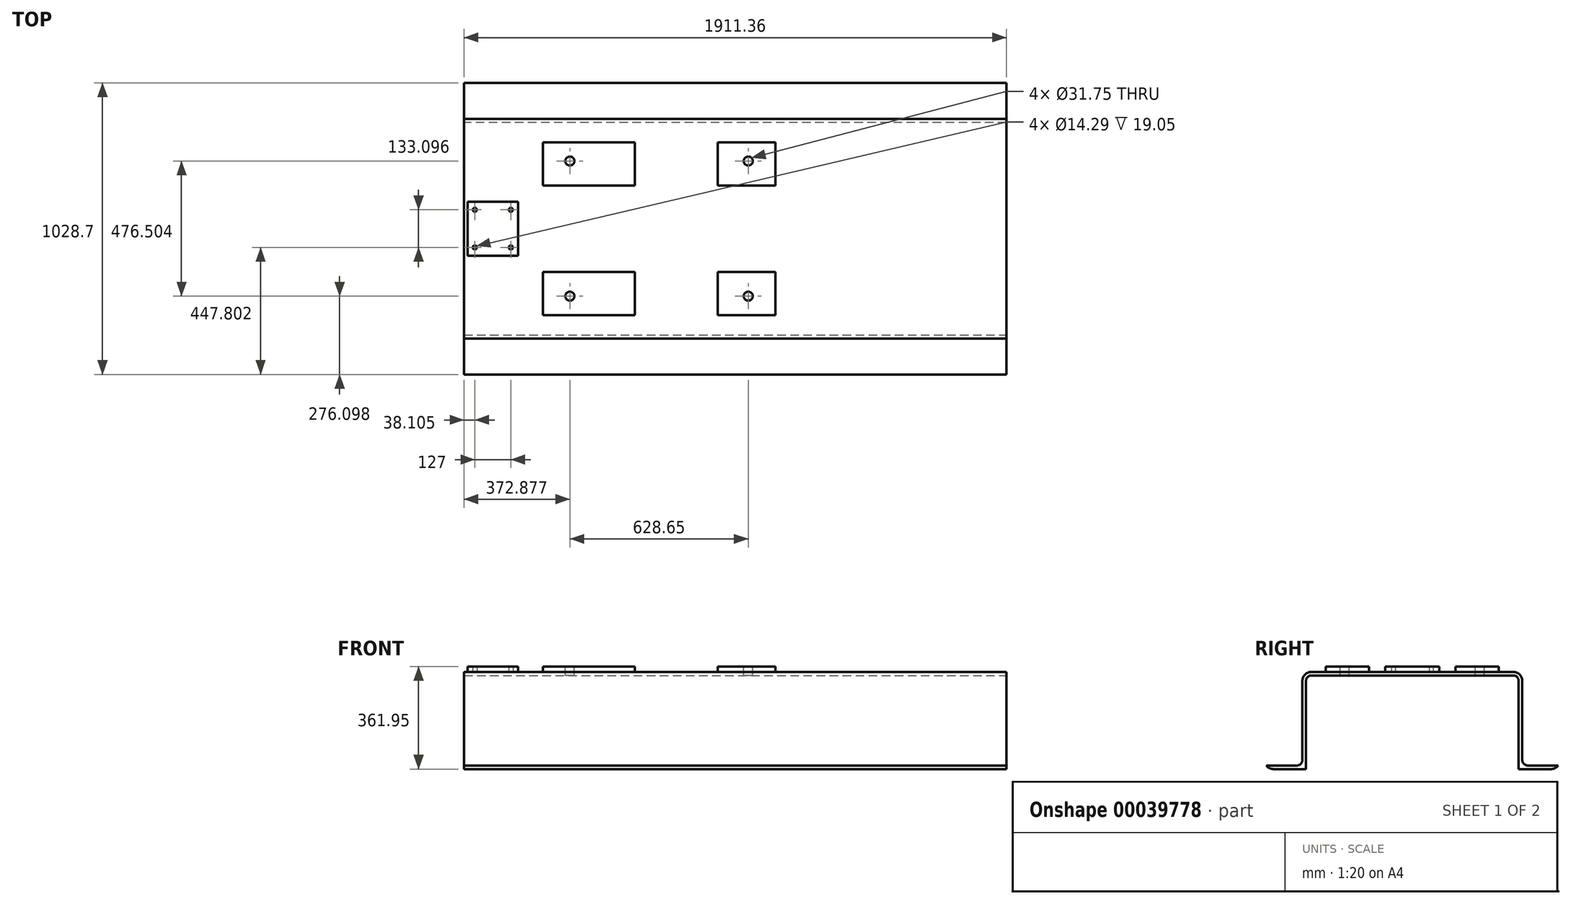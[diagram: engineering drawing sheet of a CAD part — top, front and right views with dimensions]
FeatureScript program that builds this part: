
annotation { "Feature Type Name" : "Feature", "Feature Type Description" : "" }
export const myFeature = defineFeature(function(context is Context, id is Id, definition is map)
    precondition{}
    {
        {
            var Q0;
            Q0=qCreatedBy(makeId("Top.planeOp"),FACE);
            var sketch = newSketch(context, id + "F0", { "sketchPlane" : qUnion([Q0])});
            skLineSegment(sketch, "E0.rect.bottom", {"start": v(-955.68, 387.35) * mm, "end": v(955.68, 387.35) * mm});
            skLineSegment(sketch, "E0.rect.top", {"start": v(-955.68, -387.35) * mm, "end": v(955.68, -387.35) * mm});
            skLineSegment(sketch, "E0.rect.left", {"start": v(-955.68, 387.35) * mm, "end": v(-955.68, -387.35) * mm});
            skLineSegment(sketch, "E0.rect.right", {"start": v(955.68, 387.35) * mm, "end": v(955.68, -387.35) * mm});
            skPoint(sketch, "E0.rect.middle", {"position": v(0, 0) * mm});
            skLineSegment(sketch, "E1.0", {"start": v(644.53, 387.35) * mm, "end": v(644.52, -387.35) * mm, "construction": true});
            skLineSegment(sketch, "E2.0", {"start": v(-268.35, 387.35) * mm, "end": v(-268.35, -387.35) * mm, "construction": true});
            skLineSegment(sketch, "E3.0", {"start": v(-354.2, 387.35) * mm, "end": v(-354.2, -387.35) * mm, "construction": true});
            skLineSegment(sketch, "E4.0", {"start": v(-678.05, 387.35) * mm, "end": v(-678.05, -387.35) * mm, "construction": true});
            skLineSegment(sketch, "E5.0", {"start": v(-62.1, 387.35) * mm, "end": v(-62.1, -387.35) * mm, "construction": true});
            skLineSegment(sketch, "E6.0", {"start": v(141.1, 387.35) * mm, "end": v(141.1, -387.35) * mm, "construction": true});
            skLineSegment(sketch, "E7", {"start": v(-955.68, 0) * mm, "end": v(955.68, 0) * mm, "construction": true});
            skLineSegment(sketch, "E8.0", {"start": v(-955.68, -152.4) * mm, "end": v(955.68, -152.4) * mm, "construction": true});
            skLineSegment(sketch, "E9.0", {"start": v(-955.68, -304.8) * mm, "end": v(955.68, -304.8) * mm, "construction": true});
            skLineSegment(sketch, "E10.bottom", {"start": v(-678.05, -152.4) * mm, "end": v(-354.2, -152.4) * mm});
            skLineSegment(sketch, "E10.top", {"start": v(-678.05, -304.8) * mm, "end": v(-354.2, -304.8) * mm});
            skLineSegment(sketch, "E10.left", {"start": v(-678.05, -152.4) * mm, "end": v(-678.05, -304.8) * mm});
            skLineSegment(sketch, "E10.right", {"start": v(-354.2, -152.4) * mm, "end": v(-354.2, -304.8) * mm});
            skLineSegment(sketch, "E11.bottom", {"start": v(-62.1, -152.4) * mm, "end": v(141.1, -152.4) * mm});
            skLineSegment(sketch, "E11.top", {"start": v(-62.1, -304.8) * mm, "end": v(141.1, -304.8) * mm});
            skLineSegment(sketch, "E11.left", {"start": v(-62.1, -152.4) * mm, "end": v(-62.1, -304.8) * mm});
            skLineSegment(sketch, "E11.right", {"start": v(141.1, -152.4) * mm, "end": v(141.1, -304.8) * mm});
            skLineSegment(sketch, "E12.0", {"start": v(-582.8, 387.35) * mm, "end": v(-582.8, -387.35) * mm, "construction": true});
            skLineSegment(sketch, "E13.0", {"start": v(45.85, 387.35) * mm, "end": v(45.85, -387.35) * mm, "construction": true});
            skLineSegment(sketch, "E14.0", {"start": v(-955.68, -238.25) * mm, "end": v(955.68, -238.25) * mm, "construction": true});
            skCircle(sketch, "E15", {"center": v(-582.8, -238.25) * mm, "radius": 15.88 * mm});
            skCircle(sketch, "E16", {"center": v(45.85, -238.25) * mm, "radius": 15.88 * mm});
            skLineSegment(sketch, "E17.MirrorCS", {"start": v(-354.2, 152.4) * mm, "end": v(-354.2, 304.8) * mm});
            skLineSegment(sketch, "E18.MirrorCS", {"start": v(-62.1, 304.8) * mm, "end": v(141.1, 304.8) * mm});
            skLineSegment(sketch, "E19.MirrorCS", {"start": v(141.1, 152.4) * mm, "end": v(141.1, 304.8) * mm});
            skCircle(sketch, "E20.MirrorC", {"center": v(45.85, 238.25) * mm, "radius": 15.88 * mm});
            skCircle(sketch, "E21.MirrorC", {"center": v(-582.8, 238.25) * mm, "radius": 15.88 * mm});
            skLineSegment(sketch, "E22.MirrorCS", {"start": v(-62.1, 152.4) * mm, "end": v(-62.1, 304.8) * mm});
            skLineSegment(sketch, "E23.MirrorCS", {"start": v(-678.05, 152.4) * mm, "end": v(-354.2, 152.4) * mm});
            skLineSegment(sketch, "E24.MirrorCS", {"start": v(-678.05, 152.4) * mm, "end": v(-678.05, 304.8) * mm});
            skLineSegment(sketch, "E25.MirrorCS", {"start": v(-62.1, 152.4) * mm, "end": v(141.1, 152.4) * mm});
            skLineSegment(sketch, "E26.MirrorCS", {"start": v(-678.05, 304.8) * mm, "end": v(-354.2, 304.8) * mm});
            skSolve(sketch);
        }
        {
            var Q0;
            Q0=makeQuery(id+"F0.imprint","IMPRINT",FACE,{"disambiguationData":[TD([[makeQuery(id+"F0.imprint","IMPRINT",EDGE,{"derivedFrom":sQuery(id+"F0.wireOp",EDGE,"E0.rect.bottom")}),-1.0]])]});
            var Q1;
            Q1=makeQuery(id+"F0.imprint","IMPRINT",FACE,{"disambiguationData":[TD([[makeQuery(id+"F0.imprint","IMPRINT",EDGE,{"derivedFrom":sQuery(id+"F0.wireOp",EDGE,"E17.MirrorCS")}),1.0]])]});
            var Q2;
            Q2=makeQuery(id+"F0.imprint","IMPRINT",FACE,{"disambiguationData":[TD([[makeQuery(id+"F0.imprint","IMPRINT",EDGE,{"derivedFrom":sQuery(id+"F0.wireOp",EDGE,"E10.bottom")}),-1.0]])]});
            var Q3;
            Q3=makeQuery(id+"F0.imprint","IMPRINT",FACE,{"disambiguationData":[TD([[makeQuery(id+"F0.imprint","IMPRINT",EDGE,{"derivedFrom":sQuery(id+"F0.wireOp",EDGE,"E18.MirrorCS")}),-1.0]])]});
            var Q4;
            Q4=makeQuery(id+"F0.imprint","IMPRINT",FACE,{"disambiguationData":[TD([[makeQuery(id+"F0.imprint","IMPRINT",EDGE,{"derivedFrom":sQuery(id+"F0.wireOp",EDGE,"E11.bottom")}),-1.0]])]});
            extrude(context, id + "F1", {"entities" : qUnion([Q0, Q1, Q2, Q3, Q4]), "oppositeDirection" : true, "depth" : 12.7 * mm});
        }
        {
            var Q0;
            Q0=makeQuery(id+"F0.imprint","IMPRINT",FACE,{"disambiguationData":[TD([[makeQuery(id+"F0.imprint","IMPRINT",EDGE,{"derivedFrom":sQuery(id+"F0.wireOp",EDGE,"E17.MirrorCS")}),1.0]])]});
            var Q1;
            Q1=makeQuery(id+"F0.imprint","IMPRINT",FACE,{"disambiguationData":[TD([[makeQuery(id+"F0.imprint","IMPRINT",EDGE,{"derivedFrom":sQuery(id+"F0.wireOp",EDGE,"E10.bottom")}),-1.0]])]});
            var Q2;
            Q2=makeQuery(id+"F0.imprint","IMPRINT",FACE,{"disambiguationData":[TD([[makeQuery(id+"F0.imprint","IMPRINT",EDGE,{"derivedFrom":sQuery(id+"F0.wireOp",EDGE,"E18.MirrorCS")}),-1.0]])]});
            var Q3;
            Q3=makeQuery(id+"F0.imprint","IMPRINT",FACE,{"disambiguationData":[TD([[makeQuery(id+"F0.imprint","IMPRINT",EDGE,{"derivedFrom":sQuery(id+"F0.wireOp",EDGE,"E11.bottom")}),-1.0]])]});
            extrude(context, id + "F2", {"entities" : qUnion([Q0, Q1, Q2, Q3]), "operationType" : NewBodyOperationType.ADD, "depth" : 19.05 * mm});
        }
        {
            var Q0;
            Q0=makeQuery(id+"F1.opExtrude","SWEPT_FACE",FACE,{"disambiguationData":[OSD([sQuery(id+"F0.wireOp",EDGE,"E0.rect.right")])]});
            var sketch = newSketch(context, id + "F3", { "sketchPlane" : qUnion([Q0])});
            skLineSegment(sketch, "E27.bottom", {"start": v(-387.35, 0) * mm, "end": v(-374.65, 0) * mm});
            skLineSegment(sketch, "E27.top", {"start": v(-387.35, -342.9) * mm, "end": v(-374.65, -342.9) * mm});
            skLineSegment(sketch, "E27.left", {"start": v(-387.35, 0) * mm, "end": v(-387.35, -342.9) * mm});
            skLineSegment(sketch, "E27.right", {"start": v(-374.65, 0) * mm, "end": v(-374.65, -342.9) * mm});
            skLineSegment(sketch, "E28", {"start": v(0, 0) * mm, "end": v(0, -288.05) * mm, "construction": true});
            skPoint(sketch, "E28.endSnap0", {"position": v(0, -12.7) * mm});
            skLineSegment(sketch, "E29.bottom", {"start": v(-374.65, -342.9) * mm, "end": v(-514.35, -342.9) * mm});
            skLineSegment(sketch, "E29.top", {"start": v(-374.65, -330.2) * mm, "end": v(-514.35, -330.2) * mm});
            skLineSegment(sketch, "E29.left", {"start": v(-374.65, -342.9) * mm, "end": v(-374.65, -330.2) * mm});
            skLineSegment(sketch, "E29.right", {"start": v(-514.35, -342.9) * mm, "end": v(-514.35, -330.2) * mm});
            skLineSegment(sketch, "E30.MirrorCS", {"start": v(387.35, 0) * mm, "end": v(374.65, 0) * mm});
            skLineSegment(sketch, "E31.MirrorCS", {"start": v(374.65, -342.9) * mm, "end": v(374.65, -330.2) * mm});
            skLineSegment(sketch, "E32.MirrorCS", {"start": v(387.35, -342.9) * mm, "end": v(374.65, -342.9) * mm});
            skLineSegment(sketch, "E33.MirrorCS", {"start": v(514.35, -342.9) * mm, "end": v(514.35, -330.2) * mm});
            skLineSegment(sketch, "E34.MirrorCS", {"start": v(387.35, 0) * mm, "end": v(387.35, -342.9) * mm});
            skLineSegment(sketch, "E35.MirrorCS", {"start": v(374.65, 0) * mm, "end": v(374.65, -342.9) * mm});
            skLineSegment(sketch, "E36.MirrorCS", {"start": v(374.65, -330.2) * mm, "end": v(514.35, -330.2) * mm});
            skLineSegment(sketch, "E37.MirrorCS", {"start": v(374.65, -342.9) * mm, "end": v(514.35, -342.9) * mm});
            skSolve(sketch);
        }
        {
            var Q0;
            Q0 = qSketchRegion(id + "F3", true);
            extrude(context, id + "F4", {"entities" : qUnion([Q0]), "operationType" : NewBodyOperationType.ADD, "oppositeDirection" : true, "depth" : 1911.35 * mm});
        }
        {
            var Q0;
            Q0=makeQuery(id+"F4.opExtrude","SWEPT_EDGE",EDGE,{"disambiguationData":[OSD([sQuery(id+"F3.wireOp",EDGE,"E27.left"),sQuery(id+"F3.wireOp",EDGE,"E29.top")])]});
            var Q1;
            Q1=makeQuery(id+"F4.opExtrude","SWEPT_EDGE",EDGE,{"disambiguationData":[OSD([sQuery(id+"F3.wireOp",EDGE,"E34.MirrorCS"),sQuery(id+"F3.wireOp",EDGE,"E36.MirrorCS")])]});
            var Q2;
            Q2=makeQuery(id+"F4.boolean.opBoolean","INTERSECT",EDGE,{"derivedFrom":[makeQuery(id+"F1.opExtrude","CAP_FACE",FACE,{"disambiguationData":[OSD([sQuery(id+"F0.wireOp",EDGE,"E0.rect.bottom"),sQuery(id+"F0.wireOp",EDGE,"E0.rect.top"),sQuery(id+"F0.wireOp",EDGE,"E0.rect.left"),sQuery(id+"F0.wireOp",EDGE,"E0.rect.right"),sQuery(id+"F0.wireOp",EDGE,"E15"),sQuery(id+"F0.wireOp",EDGE,"E16"),sQuery(id+"F0.wireOp",EDGE,"E20.MirrorC"),sQuery(id+"F0.wireOp",EDGE,"E21.MirrorC")])],"isStart":false}),makeQuery(id+"F4.opExtrude","SWEPT_FACE",FACE,{"disambiguationData":[OSD([sQuery(id+"F3.wireOp",EDGE,"E35.MirrorCS")])]})]});
            var Q3;
            Q3=makeQuery(id+"F4.boolean.opBoolean","INTERSECT",EDGE,{"derivedFrom":[makeQuery(id+"F1.opExtrude","CAP_FACE",FACE,{"disambiguationData":[OSD([sQuery(id+"F0.wireOp",EDGE,"E0.rect.bottom"),sQuery(id+"F0.wireOp",EDGE,"E0.rect.top"),sQuery(id+"F0.wireOp",EDGE,"E0.rect.left"),sQuery(id+"F0.wireOp",EDGE,"E0.rect.right"),sQuery(id+"F0.wireOp",EDGE,"E15"),sQuery(id+"F0.wireOp",EDGE,"E16"),sQuery(id+"F0.wireOp",EDGE,"E20.MirrorC"),sQuery(id+"F0.wireOp",EDGE,"E21.MirrorC")])],"isStart":false}),makeQuery(id+"F4.opExtrude","SWEPT_FACE",FACE,{"disambiguationData":[OSD([sQuery(id+"F3.wireOp",EDGE,"E27.right"),sQuery(id+"F3.wireOp",EDGE,"E29.left")])]})]});
            fillet(context, id + "F5", {"entities" : qUnion([Q0, Q1, Q2, Q3]), "radius" : 19.05 * mm, "tangentPropagation" : true, "allowEdgeOverflow" : false});
        }
        {
            var Q0;
            Q0=makeQuery(id+"F4.opExtrude","SWEPT_EDGE",EDGE,{"disambiguationData":[OSD([sQuery(id+"F3.wireOp",EDGE,"E35.MirrorCS"),sQuery(id+"F3.wireOp",EDGE,"E37.MirrorCS")])]});
            var Q1;
            Q1=makeQuery(id+"F4.opExtrude","SWEPT_EDGE",EDGE,{"disambiguationData":[OSD([sQuery(id+"F3.wireOp",EDGE,"E29.bottom"),sQuery(id+"F3.wireOp",EDGE,"E29.left")])]});
            var Q2;
            Q2=makeQuery(id+"F1.opExtrude","CAP_EDGE",EDGE,{"disambiguationData":[OSD([sQuery(id+"F0.wireOp",EDGE,"E0.rect.bottom")])],"isStart":true});
            var Q3;
            Q3=makeQuery(id+"F1.opExtrude","CAP_EDGE",EDGE,{"disambiguationData":[OSD([sQuery(id+"F0.wireOp",EDGE,"E0.rect.top")])],"isStart":true});
            fillet(context, id + "F6", {"entities" : qUnion([Q0, Q1, Q2, Q3]), "radius" : 31.75 * mm, "tangentPropagation" : true, "allowEdgeOverflow" : false});
        }
        {
            var Q0;
            Q0=makeQuery(id+"F0.imprint","IMPRINT",FACE,{"disambiguationData":[TD([[makeQuery(id+"F0.imprint","IMPRINT",EDGE,{"derivedFrom":sQuery(id+"F0.wireOp",EDGE,"E0.rect.bottom")}),-1.0]])]});
            var sketch = newSketch(context, id + "F7", { "sketchPlane" : qUnion([Q0])});
            skLineSegment(sketch, "E38.0", {"start": v(-268.35, 387.35) * mm, "end": v(-268.35, -387.35) * mm, "construction": true});
            skLineSegment(sketch, "E39.0", {"start": v(-678.05, 152.4) * mm, "end": v(-678.05, 304.8) * mm, "construction": true});
            skLineSegment(sketch, "E40.0", {"start": v(-765.43, 0) * mm, "end": v(955.68, 0) * mm, "construction": true});
            skLineSegment(sketch, "E41.0", {"start": v(-765.43, 0) * mm, "end": v(-765.43, 95.25) * mm});
            skLineSegment(sketch, "E42.0", {"start": v(-943.23, 0) * mm, "end": v(-943.23, 95.25) * mm});
            skLineSegment(sketch, "E43.0", {"start": v(-943.23, 95.25) * mm, "end": v(-765.43, 95.25) * mm});
            skPoint(sketch, "E44.orphan", {"position": v(-955.68, 0) * mm});
            skLineSegment(sketch, "E45.MirrorCS", {"start": v(-943.23, -95.25) * mm, "end": v(-765.43, -95.25) * mm});
            skLineSegment(sketch, "E46.MirrorCS", {"start": v(-765.43, 0) * mm, "end": v(-765.43, -95.25) * mm});
            skLineSegment(sketch, "E47.MirrorCS", {"start": v(-943.23, 0) * mm, "end": v(-943.23, -95.25) * mm});
            skPoint(sketch, "E48.orphan", {"position": v(-955.68, 95.25) * mm});
            skPoint(sketch, "E49.orphan", {"position": v(-955.68, -95.25) * mm});
            skLineSegment(sketch, "E50.0", {"start": v(-790.57, 387.35) * mm, "end": v(-790.58, -387.35) * mm, "construction": true});
            skLineSegment(sketch, "E51.0", {"start": v(-917.57, 387.35) * mm, "end": v(-917.58, -387.35) * mm, "construction": true});
            skLineSegment(sketch, "E52.0", {"start": v(-943.23, -66.55) * mm, "end": v(955.68, -66.55) * mm, "construction": true});
            skCircle(sketch, "E53", {"center": v(-917.57, -66.55) * mm, "radius": 7.14 * mm});
            skCircle(sketch, "E54", {"center": v(-790.57, -66.55) * mm, "radius": 7.14 * mm});
            skCircle(sketch, "E55.MirrorC", {"center": v(-790.57, 66.55) * mm, "radius": 7.14 * mm});
            skCircle(sketch, "E56.MirrorC", {"center": v(-917.57, 66.55) * mm, "radius": 7.14 * mm});
            skSolve(sketch);
        }
        {
            var Q0;
            Q0 = qSketchRegion(id + "F7", true);
            extrude(context, id + "F8", {"entities" : qUnion([Q0]), "operationType" : NewBodyOperationType.ADD, "depth" : 19.05 * mm});
        }
    });
